# Revit family: LineaSingola_Assieme Modulblock H13-40
name_source: partatom
category: Modelli generici
revit_build: Autodesk Revit 2016 (Build: 20161004_0715(x64)
units: mm (PartAtom-declared; Revit-internal decimal feet)

## family parameters
Basato su piano di lavoro = No
Condiviso = Sì
Punto di calcolo locali = No
Può ospitare armatura = No
Quota connettore circolare = Usa diametro
Sempre verticale = Sì
Taglio con vuoti quando caricato = No
Tipo di parte = Normale

## types (9) — shared parameters
L_geoblock = 262 mm  [stored 0.85958 ft]
L_modulo = 500 mm  [stored 1.64042 ft]

## per-type parameters (varying)
| type | H_modulo | Tipo_fermagetto | Tipo_geoblock | Tipo_modulo |
| MODULO H20 | 450 mm  [stored 1.47638 ft] | Fermagetto_Modulo : EMOFGET0020 - FERMAGETTO MODULO H20 | Geoblock Modulo H13-H70 : EMOGBLO0020 - GEOBLOCK MODULO H20 | Modulo H13-H40 : EMODULO5020 - MODULO H20 |
| MODULO H25 | 500 mm  [stored 1.64042 ft] | Fermagetto_Modulo : EMOFGET0025 - FERMAGETTO MODULO H25 | Geoblock Modulo H13-H70 : EMOGBLO0025 - GEOBLOCK MODULO H25 | Modulo H13-H40 : EMODULO5025 - MODULO H25 |
| MODULO H27 | 550 mm | Fermagetto_Modulo : EMOFGET0027 - FERMAGETTO MODULO H27 | Geoblock Modulo H13-H70 : EMOGBLO0027 - GEOBLOCK MODULO H27 | Modulo H13-H40 : EMODULO5027 - MODULO H27 |
| MODULO H30 | 600 mm | Fermagetto_Modulo : EMOFGET0030 - FERMAGETTO MODULO H30 | Geoblock Modulo H13-H70 : EMOGBLO0030 - GEOBLOCK MODULO H30 | Modulo H13-H40 : EMODULO5030 - MODULO H30 |
| MODULO H40 | 700 mm  [stored 2.29659 ft] | Fermagetto_Modulo : EMOFGET0040 - FERMAGETTO MODULO H40 | Geoblock Modulo H13-H70 : EMOGBLO0040 - GEOBLOCK MODULO H40 | Modulo H13-H40 : EMODULO5040 - MODULO H40 |
| MODULO H35 | 650 mm  [stored 2.13255 ft] | Fermagetto_Modulo : EMOFGET0035 - FERMAGETTO MODULO H35 | Geoblock Modulo H13-H70 : EMOGBLO0035 - GEOBLOCK MODULO H35 | Modulo H13-H40 : EMODULO5035 - MODULO H35 |
| MODULO H17 | 450 mm  [stored 1.47638 ft] | Fermagetto_Modulo : EMOFGET0017 - FERMAGETTO MODULO H17 | Geoblock Modulo H13-H70 : EMOGBLO0017 - GEOBLOCK MODULO H17 | Modulo H13-H40 : EMODULO5017 - MODULO H17 |
| MODULO H15 | 450 mm  [stored 1.47638 ft] | Fermagetto_Modulo : EMOFGET0015 - FERMAGETTO MODULO H15 | Geoblock Modulo H13-H70 : EMOGBLO0015 - GEOBLOCK MODULO H15 | Modulo H13-H40 : EMODULO5015 - MODULO H15 |
| MODULO H13 | 450 mm  [stored 1.47638 ft] | Fermagetto_Modulo : EMOFGET0013 - FERMAGETTO MODULO H13 | Geoblock Modulo H13-H70 : EMOGBLO0013 - GEOBLOCK MODULO H13 | Modulo H13-H40 : EMODULO5013 - MODULO H13 |

note: [stored X ft] marks values corroborated as IEEE doubles in the binary element streams (Revit-internal decimal feet)
